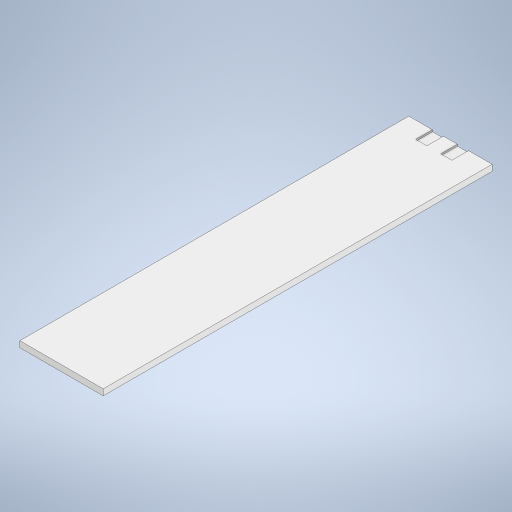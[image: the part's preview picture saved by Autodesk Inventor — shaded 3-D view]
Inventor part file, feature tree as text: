
AUTODESK INVENTOR PART (.ipt)
format: ipt  version: 2024 (Build 280153000, 153)  size: 249,344 bytes
history: native  units: mm
features: extrude x2, sketch x2
ambient origin geometry x8: Origin, YZ Plane, XZ Plane, XY Plane, X Axis, Y Axis, Z Axis, Center Point
bodies: Solide1 (feature_tree)
feature tree (4):
  extrude  "Extrusion1"  Depth=15.0mm
  extrude  "Extrusion2"  Depth=70.0mm
  sketch  "Esquisse1"
  sketch  "Esquisse2"
